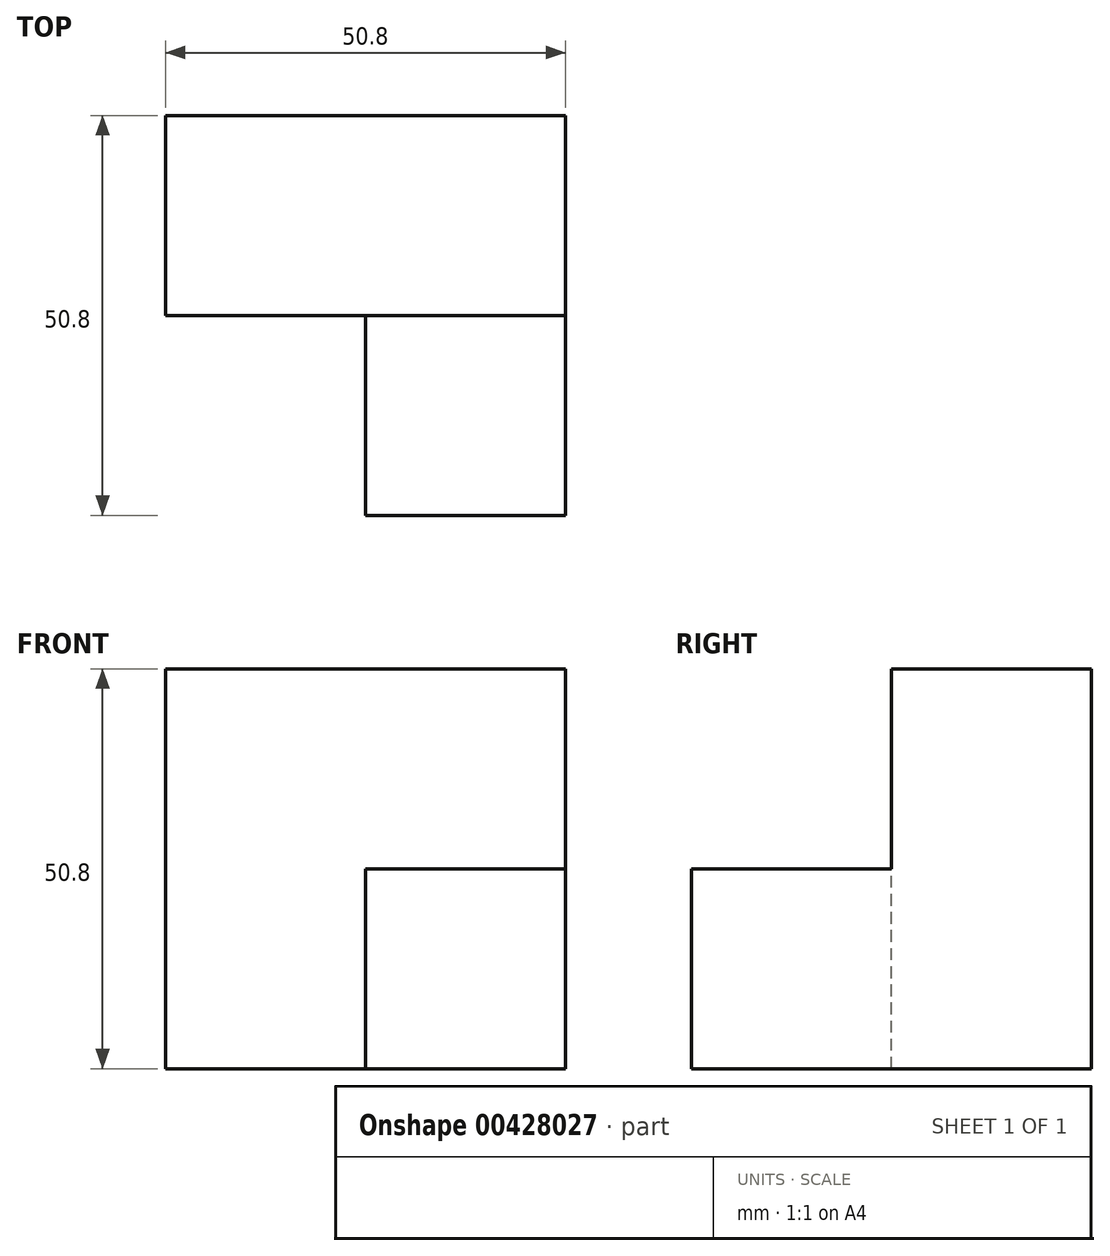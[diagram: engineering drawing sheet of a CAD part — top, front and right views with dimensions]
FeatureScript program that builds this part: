
annotation { "Feature Type Name" : "Feature", "Feature Type Description" : "" }
export const myFeature = defineFeature(function(context is Context, id is Id, definition is map)
    precondition{}
    {
        {
            var Q0;
            Q0=qCreatedBy(makeId("Front.planeOp"),FACE);
            var sketch = newSketch(context, id + "F0", { "sketchPlane" : qUnion([Q0])});
            skLineSegment(sketch, "E0", {"start": v(0, 0) * mm, "end": v(-50.8, 0) * mm});
            skLineSegment(sketch, "E1", {"start": v(-50.8, 0) * mm, "end": v(-50.8, 50.8) * mm});
            skLineSegment(sketch, "E2", {"start": v(-50.8, 41.37) * mm, "end": v(-50.8, 50.8) * mm});
            skLineSegment(sketch, "E3", {"start": v(-50.8, 50.8) * mm, "end": v(0, 50.8) * mm});
            skLineSegment(sketch, "E4", {"start": v(0, 50.8) * mm, "end": v(0, 0) * mm});
            skSolve(sketch);
        }
        {
            var Q0;
            Q0 = qSketchRegion(id + "F0", true);
            extrude(context, id + "F1", {"entities" : qUnion([Q0]), "depth" : 25.4 * mm});
        }
        {
            var Q0;
            Q0=makeQuery(id+"F1.opExtrude","CAP_FACE",FACE,{"disambiguationData":[OSD([sQuery(id+"F0.wireOp",EDGE,"E0"),sQuery(id+"F0.wireOp",EDGE,"E1"),sQuery(id+"F0.wireOp",EDGE,"E2"),sQuery(id+"F0.wireOp",EDGE,"E3"),sQuery(id+"F0.wireOp",EDGE,"E4")])],"isStart":false});
            var sketch = newSketch(context, id + "F2", { "sketchPlane" : qUnion([Q0])});
            skLineSegment(sketch, "E5.bottom", {"start": v(0, 0) * mm, "end": v(-25.4, 0) * mm});
            skLineSegment(sketch, "E5.top", {"start": v(0, 25.4) * mm, "end": v(-25.4, 25.4) * mm});
            skLineSegment(sketch, "E5.left", {"start": v(0, 0) * mm, "end": v(0, 25.4) * mm});
            skLineSegment(sketch, "E5.right", {"start": v(-25.4, 0) * mm, "end": v(-25.4, 25.4) * mm});
            skSolve(sketch);
        }
        {
            var Q0;
            Q0 = qSketchRegion(id + "F2", true);
            extrude(context, id + "F3", {"entities" : qUnion([Q0]), "operationType" : NewBodyOperationType.ADD, "depth" : 25.4 * mm});
        }
    });
